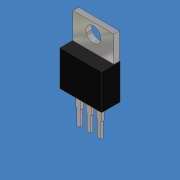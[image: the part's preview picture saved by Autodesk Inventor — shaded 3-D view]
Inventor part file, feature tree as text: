
AUTODESK INVENTOR PART (.ipt)
format: ipt  version: 2011 SP1 (Build 150282100, 282)  size: 135,680 bytes
history: native  units: mm (DEFAULTED — no unit token found)
features: sketch x5, extrude x4, hole x1, pattern_linear x1
ambient origin geometry x8: Origin, YZ Plane, XZ Plane, XY Plane, X Axis, Y Axis, Z Axis, Center Point
bodies: Solid1 (feature_tree)
feature tree (11):
  extrude  "Extrusion1"  Depth=8.636mm
  extrude  "Extrusion2"  Depth=6.35mm TaperAngle=0.0deg
  hole  "Hole1"  [1 undecoded]
  extrude  "Extrusion3"  Depth=0.5842mm
  extrude  "Extrusion4"  Depth=1.27mm
  pattern_linear  "Rectangular Pattern1"  Spacing1=1.905mm  [1 undecoded]
  sketch  "Sketch1"  dims[d0=10.16mm d1=8.636mm]
  sketch  "Sketch2"  dims[d2=4.4704mm d3=0.0mm d5=6.35mm d6=0.0mm]
  sketch  "Sketch3"  dims[d7=1.397mm d8=9.9822mm]
  sketch  "Sketch4"  dims[d9=2.54mm]
  sketch  "Sketch5"  dims[d10=3.683mm d11=12.7mm d12=9.525mm d13=6.35mm d14=14.3117mm d15=19.05mm d16=20.594885mm d17=0.5842mm d18=1.27mm d19=1.905mm d20=3.81mm d21=0.0mm d22=0.8128mm d23=3.81mm d24=0.0mm d25=30.0mm d27=2.54mm]
note: 2 required parameter values undecoded (feature->parameter linkage not recoverable at this tier; creation-order binding heuristic only, values carry confidence <= 0.55)
